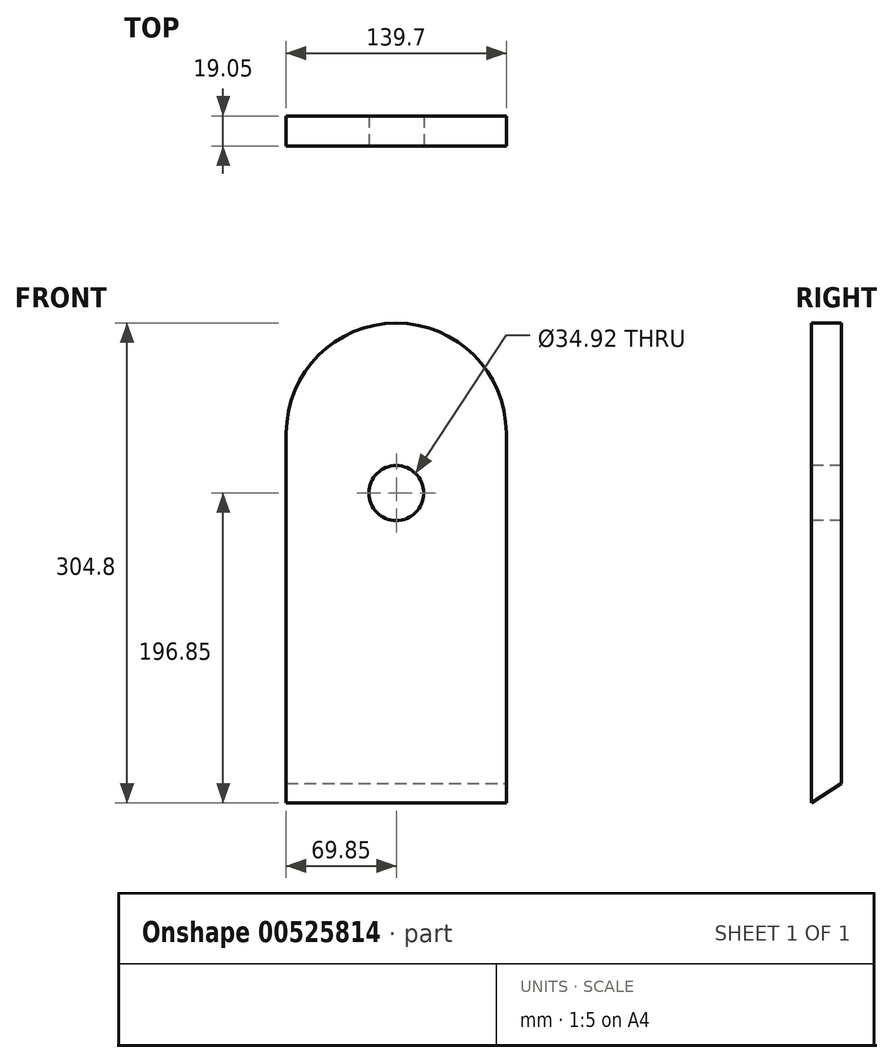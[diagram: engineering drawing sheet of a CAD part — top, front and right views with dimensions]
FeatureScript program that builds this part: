
annotation { "Feature Type Name" : "Feature", "Feature Type Description" : "" }
export const myFeature = defineFeature(function(context is Context, id is Id, definition is map)
    precondition{}
    {
        {
            var Q0;
            Q0=qCreatedBy(makeId("Front.planeOp"),FACE);
            var sketch = newSketch(context, id + "F0", { "sketchPlane" : qUnion([Q0])});
            skLineSegment(sketch, "E0", {"start": v(0, 0) * mm, "end": v(0, 234.95) * mm});
            skArc(sketch, "E1", {"start": v(139.7, 234.95) * mm, "mid": v(69.85, 304.8) * mm, "end": v(0, 234.95) * mm});
            skLineSegment(sketch, "E2", {"start": v(139.7, 234.95) * mm, "end": v(139.7, 0) * mm});
            skLineSegment(sketch, "E3", {"start": v(139.7, 0) * mm, "end": v(0, 0) * mm});
            skSolve(sketch);
        }
        {
            var Q0;
            Q0=makeQuery(id+"F0.imprint","IMPRINT",FACE,{"disambiguationData":[TD([[makeQuery(id+"F0.imprint","IMPRINT",EDGE,{"derivedFrom":sQuery(id+"F0.wireOp",EDGE,"E0")}),-1.0]])]});
            extrude(context, id + "F1", {"entities" : qUnion([Q0]), "depth" : 19.05 * mm, "offsetDistance" : 25.4 * mm});
        }
        {
            var Q0;
            Q0=makeQuery(id+"F1.opExtrude","SWEPT_FACE",FACE,{"disambiguationData":[OSD([sQuery(id+"F0.wireOp",EDGE,"E2")])]});
            var sketch = newSketch(context, id + "F2", { "sketchPlane" : qUnion([Q0])});
            skLineSegment(sketch, "E4", {"start": v(-19.05, 0) * mm, "end": v(0, 12.37) * mm});
            skLineSegment(sketch, "E5", {"start": v(0, 12.37) * mm, "end": v(0, 0) * mm});
            skLineSegment(sketch, "E6", {"start": v(0, 0) * mm, "end": v(-19.05, 0) * mm});
            skSolve(sketch);
        }
        {
            var Q0;
            Q0=makeQuery(id+"F2.imprint","IMPRINT",FACE,{"disambiguationData":[TD([[makeQuery(id+"F2.imprint","IMPRINT",EDGE,{"derivedFrom":sQuery(id+"F2.wireOp",EDGE,"E4")}),-1.0]])]});
            extrude(context, id + "F3", {"entities" : qUnion([Q0]), "operationType" : NewBodyOperationType.REMOVE, "endBound" : BoundingType.THROUGH_ALL, "oppositeDirection" : true, "depth" : 25.4 * mm, "offsetDistance" : 25.4 * mm});
        }
        {
            var Q0;
            Q0=makeQuery(id+"F1.opExtrude","CAP_FACE",FACE,{"disambiguationData":[OSD([sQuery(id+"F0.wireOp",EDGE,"E0"),sQuery(id+"F0.wireOp",EDGE,"E1"),sQuery(id+"F0.wireOp",EDGE,"E2"),sQuery(id+"F0.wireOp",EDGE,"E3")])],"isStart":false});
            var sketch = newSketch(context, id + "F4", { "sketchPlane" : qUnion([Q0])});
            skCircle(sketch, "E7", {"center": v(69.85, 196.85) * mm, "radius": 17.46 * mm});
            skPoint(sketch, "E7.centerSnap0", {"position": v(69.85, 0) * mm});
            skSolve(sketch);
        }
        {
            var Q0;
            Q0=makeQuery(id+"F4.imprint","IMPRINT",FACE,{"disambiguationData":[TD([[makeQuery(id+"F4.imprint","IMPRINT",EDGE,{"derivedFrom":sQuery(id+"F4.wireOp",EDGE,"E7")}),1.0]])]});
            extrude(context, id + "F5", {"entities" : qUnion([Q0]), "operationType" : NewBodyOperationType.REMOVE, "endBound" : BoundingType.THROUGH_ALL, "oppositeDirection" : true, "depth" : 25.4 * mm, "offsetDistance" : 25.4 * mm});
        }
    });
